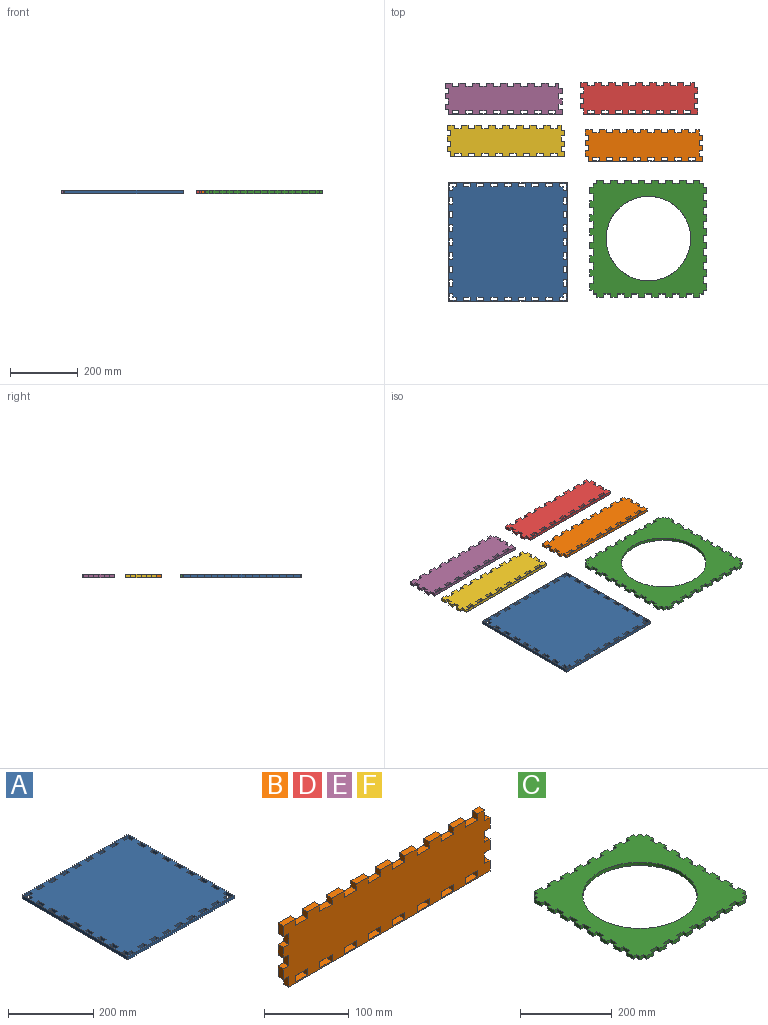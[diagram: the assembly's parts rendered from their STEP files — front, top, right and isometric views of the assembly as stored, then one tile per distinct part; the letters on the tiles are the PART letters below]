
ASSEMBLY  parts=6 mates=5
PART A: 142 faces, bbox 351x351x9 mm
  f0: plane 351x351mm, normal (0,0,1), area 116949.7mm2, adj f2,f3,f4,f5,f6,f7,f8,f9
  f1: plane 351x351mm, normal (0,0,-1), area 116949.7mm2, adj f2,f3,f4,f5,f6,f7,f8,f9
  f2: plane 11.29x9mm, normal (1,0,0), area 101.6mm2, adj f0,f1,f3,f4
  f3: plane 11.29x9mm, normal (0,1,0), area 101.6mm2, adj f0,f1,f2,f5
  f4: plane 9x9mm, normal (0,1,0), area 81mm2, adj f0,f1,f2,f110
  f5: plane 9x9mm, normal (1,0,0), area 81mm2, adj f0,f1,f3,f109
  f6: plane 20.29x9mm, normal (1,0,0), area 182.6mm2, adj f0,f1,f7,f8
  f7: plane 9x9mm, normal (0,1,0), area 81mm2, adj f0,f1,f6,f111
  f8: plane 9x9mm, normal (0,-1,0), area 81mm2, adj f0,f1,f6,f111
  f9: plane 20.29x9mm, normal (1,0,0), area 182.6mm2, adj f0,f1,f10,f11
  f10: plane 9x9mm, normal (0,1,0), area 81mm2, adj f0,f1,f9,f112
  f11: plane 9x9mm, normal (0,-1,0), area 81mm2, adj f0,f1,f9,f112
  f12: plane 20.29x9mm, normal (1,0,0), area 182.6mm2, adj f0,f1,f13,f14
  f13: plane 9x9mm, normal (0,1,0), area 81mm2, adj f0,f1,f12,f113
  f14: plane 9x9mm, normal (0,-1,0), area 81mm2, adj f0,f1,f12,f113
  f15: plane 20.29x9mm, normal (1,0,0), area 182.6mm2, adj f0,f1,f16,f17
  f16: plane 9x9mm, normal (0,1,0), area 81mm2, adj f0,f1,f15,f114
  f17: plane 9x9mm, normal (0,-1,0), area 81mm2, adj f0,f1,f15,f114
  f18: plane 20.29x9mm, normal (1,0,0), area 182.6mm2, adj f0,f1,f19,f20
  f19: plane 9x9mm, normal (0,1,0), area 81mm2, adj f0,f1,f18,f115
  f20: plane 9x9mm, normal (0,-1,0), area 81mm2, adj f0,f1,f18,f115
  f21: plane 20.29x9mm, normal (1,0,0), area 182.6mm2, adj f0,f1,f22,f23
  f22: plane 9x9mm, normal (0,1,0), area 81mm2, adj f0,f1,f21,f116
  f23: plane 9x9mm, normal (0,-1,0), area 81mm2, adj f0,f1,f21,f116
  f24: plane 20.29x9mm, normal (1,0,0), area 182.6mm2, adj f0,f1,f25,f26
  f25: plane 9x9mm, normal (0,1,0), area 81mm2, adj f0,f1,f24,f117
  f26: plane 9x9mm, normal (0,-1,0), area 81mm2, adj f0,f1,f24,f117
  f27: plane 11.29x9mm, normal (1,0,0), area 101.6mm2, adj f0,f1,f28,f30
  f28: plane 11.29x9mm, normal (0,-1,0), area 101.6mm2, adj f0,f1,f27,f29
  f29: plane 9x9mm, normal (1,0,0), area 81mm2, adj f0,f1,f28,f118
  f30: plane 9x9mm, normal (0,-1,0), area 81mm2, adj f0,f1,f27,f138
  f31: plane 11.29x9mm, normal (0,1,0), area 101.6mm2, adj f0,f1,f32,f33
  f32: plane 11.29x9mm, normal (-1,0,0), area 101.6mm2, adj f0,f1,f31,f34
  f33: plane 9x9mm, normal (-1,0,0), area 81mm2, adj f0,f1,f31,f137
  f34: plane 9x9mm, normal (0,1,0), area 81mm2, adj f0,f1,f32,f133
  f35: plane 20.29x9mm, normal (0,1,0), area 182.6mm2, adj f0,f1,f36,f37
  f36: plane 9x9mm, normal (-1,0,0), area 81mm2, adj f0,f1,f35,f102
  f37: plane 9x9mm, normal (1,0,0), area 81mm2, adj f0,f1,f35,f102
  f38: plane 20.29x9mm, normal (0,1,0), area 182.6mm2, adj f0,f1,f39,f40
  f39: plane 9x9mm, normal (-1,0,0), area 81mm2, adj f0,f1,f38,f103
  f40: plane 9x9mm, normal (1,0,0), area 81mm2, adj f0,f1,f38,f103
  f41: plane 20.29x9mm, normal (0,1,0), area 182.6mm2, adj f0,f1,f42,f43
  f42: plane 9x9mm, normal (-1,0,0), area 81mm2, adj f0,f1,f41,f104
  f43: plane 9x9mm, normal (1,0,0), area 81mm2, adj f0,f1,f41,f104
  f44: plane 20.29x9mm, normal (0,1,0), area 182.6mm2, adj f0,f1,f45,f46
  f45: plane 9x9mm, normal (-1,0,0), area 81mm2, adj f0,f1,f44,f105
  f46: plane 9x9mm, normal (1,0,0), area 81mm2, adj f0,f1,f44,f105
  f47: plane 20.29x9mm, normal (0,1,0), area 182.6mm2, adj f0,f1,f48,f49
  f48: plane 9x9mm, normal (-1,0,0), area 81mm2, adj f0,f1,f47,f106
  f49: plane 9x9mm, normal (1,0,0), area 81mm2, adj f0,f1,f47,f106
  f50: plane 20.29x9mm, normal (0,1,0), area 182.6mm2, adj f0,f1,f51,f52
  f51: plane 9x9mm, normal (-1,0,0), area 81mm2, adj f0,f1,f50,f107
  f52: plane 9x9mm, normal (1,0,0), area 81mm2, adj f0,f1,f50,f107
  f53: plane 20.29x9mm, normal (0,1,0), area 182.6mm2, adj f0,f1,f54,f55
  f54: plane 9x9mm, normal (-1,0,0), area 81mm2, adj f0,f1,f53,f108
  f55: plane 9x9mm, normal (1,0,0), area 81mm2, adj f0,f1,f53,f108
  f56: plane 20.29x9mm, normal (0,-1,0), area 182.6mm2, adj f0,f1,f57,f58
  f57: plane 9x9mm, normal (1,0,0), area 81mm2, adj f0,f1,f56,f119
  f58: plane 9x9mm, normal (-1,0,0), area 81mm2, adj f0,f1,f56,f119
  f59: plane 20.29x9mm, normal (0,-1,0), area 182.6mm2, adj f0,f1,f60,f61
  f60: plane 9x9mm, normal (1,0,0), area 81mm2, adj f0,f1,f59,f120
  f61: plane 9x9mm, normal (-1,0,0), area 81mm2, adj f0,f1,f59,f120
  f62: plane 20.29x9mm, normal (0,-1,0), area 182.6mm2, adj f0,f1,f63,f64
  f63: plane 9x9mm, normal (1,0,0), area 81mm2, adj f0,f1,f62,f121
  f64: plane 9x9mm, normal (-1,0,0), area 81mm2, adj f0,f1,f62,f121
  f65: plane 20.29x9mm, normal (0,-1,0), area 182.6mm2, adj f0,f1,f66,f67
  f66: plane 9x9mm, normal (1,0,0), area 81mm2, adj f0,f1,f65,f122
  f67: plane 9x9mm, normal (-1,0,0), area 81mm2, adj f0,f1,f65,f122
  f68: plane 20.29x9mm, normal (0,-1,0), area 182.6mm2, adj f0,f1,f69,f70
  f69: plane 9x9mm, normal (1,0,0), area 81mm2, adj f0,f1,f68,f123
  f70: plane 9x9mm, normal (-1,0,0), area 81mm2, adj f0,f1,f68,f123
  f71: plane 20.29x9mm, normal (0,-1,0), area 182.6mm2, adj f0,f1,f72,f73
  f72: plane 9x9mm, normal (1,0,0), area 81mm2, adj f0,f1,f71,f124
  f73: plane 9x9mm, normal (-1,0,0), area 81mm2, adj f0,f1,f71,f124
  f74: plane 20.29x9mm, normal (0,-1,0), area 182.6mm2, adj f0,f1,f75,f76
  f75: plane 9x9mm, normal (1,0,0), area 81mm2, adj f0,f1,f74,f125
  f76: plane 9x9mm, normal (-1,0,0), area 81mm2, adj f0,f1,f74,f125
  f77: plane 11.29x9mm, normal (0,-1,0), area 101.6mm2, adj f0,f1,f78,f80
  f78: plane 11.29x9mm, normal (-1,0,0), area 101.6mm2, adj f0,f1,f77,f79
  f79: plane 9x9mm, normal (0,-1,0), area 81mm2, adj f0,f1,f78,f140
  f80: plane 9x9mm, normal (-1,0,0), area 81mm2, adj f0,f1,f77,f139
  f81: plane 20.29x9mm, normal (-1,0,0), area 182.6mm2, adj f0,f1,f82,f83
  f82: plane 9x9mm, normal (0,-1,0), area 81mm2, adj f0,f1,f81,f126
  f83: plane 9x9mm, normal (0,1,0), area 81mm2, adj f0,f1,f81,f126
  f84: plane 20.29x9mm, normal (-1,0,0), area 182.6mm2, adj f0,f1,f85,f86
  f85: plane 9x9mm, normal (0,-1,0), area 81mm2, adj f0,f1,f84,f127
  f86: plane 9x9mm, normal (0,1,0), area 81mm2, adj f0,f1,f84,f127
  f87: plane 20.29x9mm, normal (-1,0,0), area 182.6mm2, adj f0,f1,f88,f89
  f88: plane 9x9mm, normal (0,-1,0), area 81mm2, adj f0,f1,f87,f128
  f89: plane 9x9mm, normal (0,1,0), area 81mm2, adj f0,f1,f87,f128
  f90: plane 20.29x9mm, normal (-1,0,0), area 182.6mm2, adj f0,f1,f91,f92
  f91: plane 9x9mm, normal (0,-1,0), area 81mm2, adj f0,f1,f90,f129
  f92: plane 9x9mm, normal (0,1,0), area 81mm2, adj f0,f1,f90,f129
  f93: plane 20.29x9mm, normal (-1,0,0), area 182.6mm2, adj f0,f1,f94,f95
  f94: plane 9x9mm, normal (0,-1,0), area 81mm2, adj f0,f1,f93,f130
  f95: plane 9x9mm, normal (0,1,0), area 81mm2, adj f0,f1,f93,f130
  f96: plane 20.29x9mm, normal (-1,0,0), area 182.6mm2, adj f0,f1,f97,f98
  f97: plane 9x9mm, normal (0,-1,0), area 81mm2, adj f0,f1,f96,f131
  f98: plane 9x9mm, normal (0,1,0), area 81mm2, adj f0,f1,f96,f131
  f99: plane 20.29x9mm, normal (-1,0,0), area 182.6mm2, adj f0,f1,f100,f101
  f100: plane 9x9mm, normal (0,1,0), area 81mm2, adj f0,f1,f99,f132
  f101: plane 9x9mm, normal (0,-1,0), area 81mm2, adj f0,f1,f99,f132
  f102: plane 20.29x9mm, normal (0,-1,0), area 182.6mm2, adj f0,f1,f36,f37
  f103: plane 20.29x9mm, normal (0,-1,0), area 182.6mm2, adj f0,f1,f39,f40
  f104: plane 20.29x9mm, normal (0,-1,0), area 182.6mm2, adj f0,f1,f42,f43
  f105: plane 20.29x9mm, normal (0,-1,0), area 182.6mm2, adj f0,f1,f45,f46
  f106: plane 20.29x9mm, normal (0,-1,0), area 182.6mm2, adj f0,f1,f48,f49
  f107: plane 20.29x9mm, normal (0,-1,0), area 182.6mm2, adj f0,f1,f51,f52
  f108: plane 20.29x9mm, normal (0,-1,0), area 182.6mm2, adj f0,f1,f54,f55
  f109: plane 20.29x9mm, normal (0,-1,0), area 182.6mm2, adj f0,f1,f5,f110
  f110: plane 20.29x9mm, normal (-1,0,0), area 182.6mm2, adj f0,f1,f4,f109
  f111: plane 20.29x9mm, normal (-1,0,0), area 182.6mm2, adj f0,f1,f7,f8
  f112: plane 20.29x9mm, normal (-1,0,0), area 182.6mm2, adj f0,f1,f10,f11
  f113: plane 20.29x9mm, normal (-1,0,0), area 182.6mm2, adj f0,f1,f13,f14
  f114: plane 20.29x9mm, normal (-1,0,0), area 182.6mm2, adj f0,f1,f16,f17
  f115: plane 20.29x9mm, normal (-1,0,0), area 182.6mm2, adj f0,f1,f19,f20
  f116: plane 20.29x9mm, normal (-1,0,0), area 182.6mm2, adj f0,f1,f22,f23
  f117: plane 20.29x9mm, normal (-1,0,0), area 182.6mm2, adj f0,f1,f25,f26
  f118: plane 20.29x9mm, normal (0,1,0), area 182.6mm2, adj f0,f1,f29,f138
  f119: plane 20.29x9mm, normal (0,1,0), area 182.6mm2, adj f0,f1,f57,f58
  f120: plane 20.29x9mm, normal (0,1,0), area 182.6mm2, adj f0,f1,f60,f61
  f121: plane 20.29x9mm, normal (0,1,0), area 182.6mm2, adj f0,f1,f63,f64
  f122: plane 20.29x9mm, normal (0,1,0), area 182.6mm2, adj f0,f1,f66,f67
  f123: plane 20.29x9mm, normal (0,1,0), area 182.6mm2, adj f0,f1,f69,f70
  f124: plane 20.29x9mm, normal (0,1,0), area 182.6mm2, adj f0,f1,f72,f73
  f125: plane 20.29x9mm, normal (0,1,0), area 182.6mm2, adj f0,f1,f75,f76
  f126: plane 20.29x9mm, normal (1,0,0), area 182.6mm2, adj f0,f1,f82,f83
  f127: plane 20.29x9mm, normal (1,0,0), area 182.6mm2, adj f0,f1,f85,f86
  f128: plane 20.29x9mm, normal (1,0,0), area 182.6mm2, adj f0,f1,f88,f89
  f129: plane 20.29x9mm, normal (1,0,0), area 182.6mm2, adj f0,f1,f91,f92
  f130: plane 20.29x9mm, normal (1,0,0), area 182.6mm2, adj f0,f1,f94,f95
  f131: plane 20.29x9mm, normal (1,0,0), area 182.6mm2, adj f0,f1,f97,f98
  f132: plane 20.29x9mm, normal (1,0,0), area 182.6mm2, adj f0,f1,f100,f101
  f133: plane 20.29x9mm, normal (1,0,0), area 182.6mm2, adj f0,f1,f34,f137
  f134: plane 351x9mm, normal (0,1,0), area 3159mm2, adj f0,f1,f135,f141
  f135: plane 351x9mm, normal (-1,0,0), area 3159mm2, adj f0,f1,f134,f136
  f136: plane 351x9mm, normal (0,-1,0), area 3159mm2, adj f0,f1,f135,f141
  f137: plane 20.29x9mm, normal (0,-1,0), area 182.6mm2, adj f0,f1,f33,f133
  f138: plane 20.29x9mm, normal (-1,0,0), area 182.6mm2, adj f0,f1,f30,f118
  f139: plane 20.29x9mm, normal (0,1,0), area 182.6mm2, adj f0,f1,f80,f140
  f140: plane 20.29x9mm, normal (1,0,0), area 182.6mm2, adj f0,f1,f79,f139
  f141: plane 351x9mm, normal (1,0,0), area 3159mm2, adj f0,f1,f134,f136
PART B: 90 faces, bbox 345.4x9x93.2 mm
  f0: plane 345.4x93.2mm, normal (0,-1,0), area 28379mm2, adj f1,f2,f3,f4,f5,f6,f7,f8
  f1: plane 15.7x9mm, normal (-1,0,0), area 141.3mm2, adj f0,f2,f56,f57
  f2: plane 9.2x9mm, normal (0,0,-1), area 82.8mm2, adj f0,f1,f3,f57
  f3: plane 15.5x9mm, normal (-1,0,0), area 139.5mm2, adj f0,f2,f4,f57
  f4: plane 9.2x9mm, normal (0,0,1), area 82.8mm2, adj f0,f3,f5,f57
  f5: plane 15.5x9mm, normal (-1,0,0), area 139.5mm2, adj f0,f4,f6,f57
  f6: plane 9.2x9mm, normal (0,0,-1), area 82.8mm2, adj f0,f5,f7,f57
  f7: plane 15.5x9mm, normal (-1,0,0), area 139.5mm2, adj f0,f6,f8,f57
  f8: plane 9.2x9mm, normal (0,0,1), area 82.8mm2, adj f0,f7,f9,f57
  f9: plane 15.5x9mm, normal (-1,0,0), area 139.5mm2, adj f0,f8,f10,f57
  f10: plane 9.2x9mm, normal (0,0,-1), area 82.8mm2, adj f0,f9,f11,f57
  f11: plane 15.5x9mm, normal (-1,0,0), area 139.5mm2, adj f0,f10,f12,f57
  f12: plane 336.2x9mm, normal (0,0,-1), area 3025.8mm2, adj f0,f11,f13,f57
  f13: plane 15.5x9mm, normal (1,0,0), area 139.5mm2, adj f0,f12,f14,f57
  f14: plane 9.2x9mm, normal (0,0,1), area 82.8mm2, adj f0,f13,f15,f57
  f15: plane 15.5x9mm, normal (1,0,0), area 139.5mm2, adj f0,f14,f16,f57
  f16: plane 9.2x9mm, normal (0,0,-1), area 82.8mm2, adj f0,f15,f17,f57
  f17: plane 15.5x9mm, normal (1,0,0), area 139.5mm2, adj f0,f16,f18,f57
  f18: plane 9.2x9mm, normal (0,0,1), area 82.8mm2, adj f0,f17,f19,f57
  f19: plane 15.5x9mm, normal (1,0,0), area 139.5mm2, adj f0,f18,f20,f57
  f20: plane 9.2x9mm, normal (0,0,-1), area 82.8mm2, adj f0,f19,f21,f57
  f21: plane 15.5x9mm, normal (1,0,0), area 139.5mm2, adj f0,f20,f22,f57
  f22: plane 9.2x9mm, normal (0,0,1), area 82.8mm2, adj f0,f21,f23,f57
  f23: plane 15.7x9mm, normal (1,0,0), area 141.3mm2, adj f0,f22,f24,f57
  f24: plane 11.29x9mm, normal (0,0,1), area 101.6mm2, adj f0,f23,f25,f57
  f25: plane 9.2x9mm, normal (-1,0,0), area 82.8mm2, adj f0,f24,f26,f57
  f26: plane 20.29x9mm, normal (0,0,1), area 182.6mm2, adj f0,f25,f27,f57
  f27: plane 9.2x9mm, normal (1,0,0), area 82.8mm2, adj f0,f26,f28,f57
  f28: plane 20.29x9mm, normal (0,0,1), area 182.6mm2, adj f0,f27,f29,f57
  f29: plane 9.2x9mm, normal (-1,0,0), area 82.8mm2, adj f0,f28,f30,f57
  f30: plane 20.29x9mm, normal (0,0,1), area 182.6mm2, adj f0,f29,f31,f57
  f31: plane 9.2x9mm, normal (1,0,0), area 82.8mm2, adj f0,f30,f32,f57
  f32: plane 20.29x9mm, normal (0,0,1), area 182.6mm2, adj f0,f31,f33,f57
  f33: plane 9.2x9mm, normal (-1,0,0), area 82.8mm2, adj f0,f32,f34,f57
  f34: plane 20.29x9mm, normal (0,0,1), area 182.6mm2, adj f0,f33,f35,f57
  f35: plane 9.2x9mm, normal (1,0,0), area 82.8mm2, adj f0,f34,f36,f57
  f36: plane 20.29x9mm, normal (0,0,1), area 182.6mm2, adj f0,f35,f37,f57
  f37: plane 9.2x9mm, normal (-1,0,0), area 82.8mm2, adj f0,f36,f38,f57
  f38: plane 20.29x9mm, normal (0,0,1), area 182.6mm2, adj f0,f37,f39,f57
  f39: plane 9.2x9mm, normal (1,0,0), area 82.8mm2, adj f0,f38,f40,f57
  f40: plane 20.29x9mm, normal (0,0,1), area 182.6mm2, adj f0,f39,f41,f57
  f41: plane 9.2x9mm, normal (-1,0,0), area 82.8mm2, adj f0,f40,f42,f57
  f42: plane 20.29x9mm, normal (0,0,1), area 182.6mm2, adj f0,f41,f43,f57
  f43: plane 9.2x9mm, normal (1,0,0), area 82.8mm2, adj f0,f42,f44,f57
  f44: plane 20.29x9mm, normal (0,0,1), area 182.6mm2, adj f0,f43,f45,f57
  f45: plane 9.2x9mm, normal (-1,0,0), area 82.8mm2, adj f0,f44,f46,f57
  f46: plane 20.29x9mm, normal (0,0,1), area 182.6mm2, adj f0,f45,f47,f57
  f47: plane 9.2x9mm, normal (1,0,0), area 82.8mm2, adj f0,f46,f48,f57
  f48: plane 20.29x9mm, normal (0,0,1), area 182.6mm2, adj f0,f47,f49,f57
  f49: plane 9.2x9mm, normal (-1,0,0), area 82.8mm2, adj f0,f48,f50,f57
  f50: plane 20.29x9mm, normal (0,0,1), area 182.6mm2, adj f0,f49,f51,f57
  f51: plane 9.2x9mm, normal (1,0,0), area 82.8mm2, adj f0,f50,f52,f57
  f52: plane 20.29x9mm, normal (0,0,1), area 182.6mm2, adj f0,f51,f53,f57
  f53: plane 9.2x9mm, normal (-1,0,0), area 82.8mm2, adj f0,f52,f54,f57
  f54: plane 20.29x9mm, normal (0,0,1), area 182.6mm2, adj f0,f53,f55,f57
  f55: plane 9.2x9mm, normal (1,0,0), area 82.8mm2, adj f0,f54,f56,f57
  f56: plane 20.49x9mm, normal (0,0,1), area 184.4mm2, adj f0,f1,f55,f57
  f57: plane 345.4x93.2mm, normal (0,1,0), area 28379mm2, adj f1,f2,f3,f4,f5,f6,f7,f8
  f58: plane 9x9mm, normal (-1,0,0), area 81mm2, adj f0,f57,f60,f61
  f59: plane 9x9mm, normal (1,0,0), area 81mm2, adj f0,f57,f60,f61
  f60: plane 20.29x9mm, normal (0,0,1), area 182.6mm2, adj f0,f57,f58,f59
  f61: plane 20.29x9mm, normal (0,0,-1), area 182.6mm2, adj f0,f57,f58,f59
  f62: plane 9x9mm, normal (-1,0,0), area 81mm2, adj f0,f57,f64,f65
  f63: plane 9x9mm, normal (1,0,0), area 81mm2, adj f0,f57,f64,f65
  f64: plane 20.29x9mm, normal (0,0,1), area 182.6mm2, adj f0,f57,f62,f63
  f65: plane 20.29x9mm, normal (0,0,-1), area 182.6mm2, adj f0,f57,f62,f63
  f66: plane 9x9mm, normal (-1,0,0), area 81mm2, adj f0,f57,f68,f69
  f67: plane 9x9mm, normal (1,0,0), area 81mm2, adj f0,f57,f68,f69
  f68: plane 20.29x9mm, normal (0,0,1), area 182.6mm2, adj f0,f57,f66,f67
  f69: plane 20.29x9mm, normal (0,0,-1), area 182.6mm2, adj f0,f57,f66,f67
  f70: plane 9x9mm, normal (-1,0,0), area 81mm2, adj f0,f57,f72,f73
  f71: plane 9x9mm, normal (1,0,0), area 81mm2, adj f0,f57,f72,f73
  f72: plane 20.29x9mm, normal (0,0,1), area 182.6mm2, adj f0,f57,f70,f71
  f73: plane 20.29x9mm, normal (0,0,-1), area 182.6mm2, adj f0,f57,f70,f71
  f74: plane 9x9mm, normal (-1,0,0), area 81mm2, adj f0,f57,f76,f77
  f75: plane 9x9mm, normal (1,0,0), area 81mm2, adj f0,f57,f76,f77
  f76: plane 20.29x9mm, normal (0,0,1), area 182.6mm2, adj f0,f57,f74,f75
  f77: plane 20.29x9mm, normal (0,0,-1), area 182.6mm2, adj f0,f57,f74,f75
  f78: plane 9x9mm, normal (-1,0,0), area 81mm2, adj f0,f57,f80,f81
  f79: plane 9x9mm, normal (1,0,0), area 81mm2, adj f0,f57,f80,f81
  f80: plane 20.29x9mm, normal (0,0,1), area 182.6mm2, adj f0,f57,f78,f79
  f81: plane 20.29x9mm, normal (0,0,-1), area 182.6mm2, adj f0,f57,f78,f79
  f82: plane 9x9mm, normal (-1,0,0), area 81mm2, adj f0,f57,f84,f85
  f83: plane 9x9mm, normal (1,0,0), area 81mm2, adj f0,f57,f84,f85
  f84: plane 20.29x9mm, normal (0,0,1), area 182.6mm2, adj f0,f57,f82,f83
  f85: plane 20.29x9mm, normal (0,0,-1), area 182.6mm2, adj f0,f57,f82,f83
  f86: plane 20.29x9mm, normal (0,0,-1), area 182.6mm2, adj f0,f57,f88,f89
  f87: plane 20.29x9mm, normal (0,0,1), area 182.6mm2, adj f0,f57,f88,f89
  f88: plane 9x9mm, normal (-1,0,0), area 81mm2, adj f0,f57,f86,f87
  f89: plane 9x9mm, normal (1,0,0), area 81mm2, adj f0,f57,f86,f87
PART C: 135 faces, bbox 345.4x345.4x9 mm
  f0: plane 20.29x9mm, normal (1,0,0), area 182.6mm2, adj f32,f33,f36,f40
  f1: plane 20.29x9mm, normal (1,0,0), area 182.6mm2, adj f32,f33,f39,f43
  f2: plane 20.29x9mm, normal (1,0,0), area 182.6mm2, adj f32,f33,f42,f46
  f3: plane 20.29x9mm, normal (1,0,0), area 182.6mm2, adj f32,f33,f45,f49
  f4: plane 20.29x9mm, normal (1,0,0), area 182.6mm2, adj f32,f33,f48,f52
  f5: plane 20.29x9mm, normal (1,0,0), area 182.6mm2, adj f32,f33,f51,f55
  f6: plane 20.29x9mm, normal (1,0,0), area 182.6mm2, adj f32,f33,f54,f58
  f7: plane 20.29x9mm, normal (1,0,0), area 182.6mm2, adj f32,f33,f57,f62
  f8: plane 20.29x9mm, normal (0,1,0), area 182.6mm2, adj f32,f33,f65,f69
  f9: plane 20.29x9mm, normal (0,1,0), area 182.6mm2, adj f32,f33,f68,f72
  f10: plane 20.29x9mm, normal (0,1,0), area 182.6mm2, adj f32,f33,f71,f75
  f11: plane 20.29x9mm, normal (0,1,0), area 182.6mm2, adj f32,f33,f74,f78
  f12: plane 20.29x9mm, normal (0,1,0), area 182.6mm2, adj f32,f33,f77,f81
  f13: plane 20.29x9mm, normal (0,1,0), area 182.6mm2, adj f32,f33,f80,f84
  f14: plane 20.29x9mm, normal (0,1,0), area 182.6mm2, adj f32,f33,f83,f87
  f15: plane 20.29x9mm, normal (0,1,0), area 182.6mm2, adj f32,f33,f37,f86
  f16: plane 20.29x9mm, normal (-1,0,0), area 182.6mm2, adj f32,f33,f111,f115
  f17: plane 20.29x9mm, normal (-1,0,0), area 182.6mm2, adj f32,f33,f114,f118
  f18: plane 20.29x9mm, normal (-1,0,0), area 182.6mm2, adj f32,f33,f117,f121
  f19: plane 20.29x9mm, normal (-1,0,0), area 182.6mm2, adj f32,f33,f120,f124
  f20: plane 20.29x9mm, normal (-1,0,0), area 182.6mm2, adj f32,f33,f123,f127
  f21: plane 20.29x9mm, normal (-1,0,0), area 182.6mm2, adj f32,f33,f126,f130
  f22: plane 20.29x9mm, normal (-1,0,0), area 182.6mm2, adj f32,f33,f129,f132
  f23: plane 20.29x9mm, normal (-1,0,0), area 182.6mm2, adj f32,f33,f66,f133
  f24: plane 20.29x9mm, normal (0,-1,0), area 182.6mm2, adj f32,f33,f61,f90
  f25: plane 20.29x9mm, normal (0,-1,0), area 182.6mm2, adj f32,f33,f89,f93
  f26: plane 20.29x9mm, normal (0,-1,0), area 182.6mm2, adj f32,f33,f92,f96
  f27: plane 20.29x9mm, normal (0,-1,0), area 182.6mm2, adj f32,f33,f95,f99
  f28: plane 20.29x9mm, normal (0,-1,0), area 182.6mm2, adj f32,f33,f98,f102
  f29: plane 20.29x9mm, normal (0,-1,0), area 182.6mm2, adj f32,f33,f101,f105
  f30: plane 20.29x9mm, normal (0,-1,0), area 182.6mm2, adj f32,f33,f104,f108
  f31: plane 20.29x9mm, normal (0,-1,0), area 182.6mm2, adj f32,f33,f107,f112
  f32: plane 345.4x345.4mm, normal (0,0,1), area 63816.2mm2, adj f0,f1,f2,f3,f4,f5,f6,f7
  f33: plane 345.4x345.4mm, normal (0,0,-1), area 63816.2mm2, adj f0,f1,f2,f3,f4,f5,f6,f7
  f34: plane 11.29x9mm, normal (1,0,0), area 101.6mm2, adj f32,f33,f35,f36
  f35: plane 11.29x9mm, normal (0,1,0), area 101.6mm2, adj f32,f33,f34,f37
  f36: plane 9.2x9mm, normal (0,1,0), area 82.8mm2, adj f0,f32,f33,f34
  f37: plane 9.2x9mm, normal (1,0,0), area 82.8mm2, adj f15,f32,f33,f35
  f38: plane 20.29x9mm, normal (1,0,0), area 182.6mm2, adj f32,f33,f39,f40
  f39: plane 9.2x9mm, normal (0,1,0), area 82.8mm2, adj f1,f32,f33,f38
  f40: plane 9.2x9mm, normal (0,-1,0), area 82.8mm2, adj f0,f32,f33,f38
  f41: plane 20.29x9mm, normal (1,0,0), area 182.6mm2, adj f32,f33,f42,f43
  f42: plane 9.2x9mm, normal (0,1,0), area 82.8mm2, adj f2,f32,f33,f41
  f43: plane 9.2x9mm, normal (0,-1,0), area 82.8mm2, adj f1,f32,f33,f41
  f44: plane 20.29x9mm, normal (1,0,0), area 182.6mm2, adj f32,f33,f45,f46
  f45: plane 9.2x9mm, normal (0,1,0), area 82.8mm2, adj f3,f32,f33,f44
  f46: plane 9.2x9mm, normal (0,-1,0), area 82.8mm2, adj f2,f32,f33,f44
  f47: plane 20.29x9mm, normal (1,0,0), area 182.6mm2, adj f32,f33,f48,f49
  f48: plane 9.2x9mm, normal (0,1,0), area 82.8mm2, adj f4,f32,f33,f47
  f49: plane 9.2x9mm, normal (0,-1,0), area 82.8mm2, adj f3,f32,f33,f47
  f50: plane 20.29x9mm, normal (1,0,0), area 182.6mm2, adj f32,f33,f51,f52
  f51: plane 9.2x9mm, normal (0,1,0), area 82.8mm2, adj f5,f32,f33,f50
  f52: plane 9.2x9mm, normal (0,-1,0), area 82.8mm2, adj f4,f32,f33,f50
  f53: plane 20.29x9mm, normal (1,0,0), area 182.6mm2, adj f32,f33,f54,f55
  f54: plane 9.2x9mm, normal (0,1,0), area 82.8mm2, adj f6,f32,f33,f53
  f55: plane 9.2x9mm, normal (0,-1,0), area 82.8mm2, adj f5,f32,f33,f53
  f56: plane 20.29x9mm, normal (1,0,0), area 182.6mm2, adj f32,f33,f57,f58
  f57: plane 9.2x9mm, normal (0,1,0), area 82.8mm2, adj f7,f32,f33,f56
  f58: plane 9.2x9mm, normal (0,-1,0), area 82.8mm2, adj f6,f32,f33,f56
  f59: plane 11.29x9mm, normal (1,0,0), area 101.6mm2, adj f32,f33,f60,f62
  f60: plane 11.29x9mm, normal (0,-1,0), area 101.6mm2, adj f32,f33,f59,f61
  f61: plane 9.2x9mm, normal (1,0,0), area 82.8mm2, adj f24,f32,f33,f60
  f62: plane 9.2x9mm, normal (0,-1,0), area 82.8mm2, adj f7,f32,f33,f59
  f63: plane 11.29x9mm, normal (0,1,0), area 101.6mm2, adj f32,f33,f64,f65
  f64: plane 11.29x9mm, normal (-1,0,0), area 101.6mm2, adj f32,f33,f63,f66
  f65: plane 9.2x9mm, normal (-1,0,0), area 82.8mm2, adj f8,f32,f33,f63
  f66: plane 9.2x9mm, normal (0,1,0), area 82.8mm2, adj f23,f32,f33,f64
  f67: plane 20.29x9mm, normal (0,1,0), area 182.6mm2, adj f32,f33,f68,f69
  f68: plane 9.2x9mm, normal (-1,0,0), area 82.8mm2, adj f9,f32,f33,f67
  f69: plane 9.2x9mm, normal (1,0,0), area 82.8mm2, adj f8,f32,f33,f67
  f70: plane 20.29x9mm, normal (0,1,0), area 182.6mm2, adj f32,f33,f71,f72
  f71: plane 9.2x9mm, normal (-1,0,0), area 82.8mm2, adj f10,f32,f33,f70
  f72: plane 9.2x9mm, normal (1,0,0), area 82.8mm2, adj f9,f32,f33,f70
  f73: plane 20.29x9mm, normal (0,1,0), area 182.6mm2, adj f32,f33,f74,f75
  f74: plane 9.2x9mm, normal (-1,0,0), area 82.8mm2, adj f11,f32,f33,f73
  f75: plane 9.2x9mm, normal (1,0,0), area 82.8mm2, adj f10,f32,f33,f73
  f76: plane 20.29x9mm, normal (0,1,0), area 182.6mm2, adj f32,f33,f77,f78
  f77: plane 9.2x9mm, normal (-1,0,0), area 82.8mm2, adj f12,f32,f33,f76
  f78: plane 9.2x9mm, normal (1,0,0), area 82.8mm2, adj f11,f32,f33,f76
  f79: plane 20.29x9mm, normal (0,1,0), area 182.6mm2, adj f32,f33,f80,f81
  f80: plane 9.2x9mm, normal (-1,0,0), area 82.8mm2, adj f13,f32,f33,f79
  f81: plane 9.2x9mm, normal (1,0,0), area 82.8mm2, adj f12,f32,f33,f79
  f82: plane 20.29x9mm, normal (0,1,0), area 182.6mm2, adj f32,f33,f83,f84
  f83: plane 9.2x9mm, normal (-1,0,0), area 82.8mm2, adj f14,f32,f33,f82
  f84: plane 9.2x9mm, normal (1,0,0), area 82.8mm2, adj f13,f32,f33,f82
  f85: plane 20.29x9mm, normal (0,1,0), area 182.6mm2, adj f32,f33,f86,f87
  f86: plane 9.2x9mm, normal (-1,0,0), area 82.8mm2, adj f15,f32,f33,f85
  f87: plane 9.2x9mm, normal (1,0,0), area 82.8mm2, adj f14,f32,f33,f85
  f88: plane 20.29x9mm, normal (0,-1,0), area 182.6mm2, adj f32,f33,f89,f90
  f89: plane 9.2x9mm, normal (1,0,0), area 82.8mm2, adj f25,f32,f33,f88
  f90: plane 9.2x9mm, normal (-1,0,0), area 82.8mm2, adj f24,f32,f33,f88
  f91: plane 20.29x9mm, normal (0,-1,0), area 182.6mm2, adj f32,f33,f92,f93
  f92: plane 9.2x9mm, normal (1,0,0), area 82.8mm2, adj f26,f32,f33,f91
  f93: plane 9.2x9mm, normal (-1,0,0), area 82.8mm2, adj f25,f32,f33,f91
  f94: plane 20.29x9mm, normal (0,-1,0), area 182.6mm2, adj f32,f33,f95,f96
  f95: plane 9.2x9mm, normal (1,0,0), area 82.8mm2, adj f27,f32,f33,f94
  f96: plane 9.2x9mm, normal (-1,0,0), area 82.8mm2, adj f26,f32,f33,f94
  f97: plane 20.29x9mm, normal (0,-1,0), area 182.6mm2, adj f32,f33,f98,f99
  f98: plane 9.2x9mm, normal (1,0,0), area 82.8mm2, adj f28,f32,f33,f97
  f99: plane 9.2x9mm, normal (-1,0,0), area 82.8mm2, adj f27,f32,f33,f97
  f100: plane 20.29x9mm, normal (0,-1,0), area 182.6mm2, adj f32,f33,f101,f102
  f101: plane 9.2x9mm, normal (1,0,0), area 82.8mm2, adj f29,f32,f33,f100
  f102: plane 9.2x9mm, normal (-1,0,0), area 82.8mm2, adj f28,f32,f33,f100
  f103: plane 20.29x9mm, normal (0,-1,0), area 182.6mm2, adj f32,f33,f104,f105
  f104: plane 9.2x9mm, normal (1,0,0), area 82.8mm2, adj f30,f32,f33,f103
  f105: plane 9.2x9mm, normal (-1,0,0), area 82.8mm2, adj f29,f32,f33,f103
  f106: plane 20.29x9mm, normal (0,-1,0), area 182.6mm2, adj f32,f33,f107,f108
  f107: plane 9.2x9mm, normal (1,0,0), area 82.8mm2, adj f31,f32,f33,f106
  f108: plane 9.2x9mm, normal (-1,0,0), area 82.8mm2, adj f30,f32,f33,f106
  f109: plane 11.29x9mm, normal (0,-1,0), area 101.6mm2, adj f32,f33,f110,f112
  f110: plane 11.29x9mm, normal (-1,0,0), area 101.6mm2, adj f32,f33,f109,f111
  f111: plane 9.2x9mm, normal (0,-1,0), area 82.8mm2, adj f16,f32,f33,f110
  f112: plane 9.2x9mm, normal (-1,0,0), area 82.8mm2, adj f31,f32,f33,f109
  f113: plane 20.29x9mm, normal (-1,0,0), area 182.6mm2, adj f32,f33,f114,f115
  f114: plane 9.2x9mm, normal (0,-1,0), area 82.8mm2, adj f17,f32,f33,f113
  f115: plane 9.2x9mm, normal (0,1,0), area 82.8mm2, adj f16,f32,f33,f113
  f116: plane 20.29x9mm, normal (-1,0,0), area 182.6mm2, adj f32,f33,f117,f118
  f117: plane 9.2x9mm, normal (0,-1,0), area 82.8mm2, adj f18,f32,f33,f116
  f118: plane 9.2x9mm, normal (0,1,0), area 82.8mm2, adj f17,f32,f33,f116
  f119: plane 20.29x9mm, normal (-1,0,0), area 182.6mm2, adj f32,f33,f120,f121
  f120: plane 9.2x9mm, normal (0,-1,0), area 82.8mm2, adj f19,f32,f33,f119
  f121: plane 9.2x9mm, normal (0,1,0), area 82.8mm2, adj f18,f32,f33,f119
  f122: plane 20.29x9mm, normal (-1,0,0), area 182.6mm2, adj f32,f33,f123,f124
  f123: plane 9.2x9mm, normal (0,-1,0), area 82.8mm2, adj f20,f32,f33,f122
  f124: plane 9.2x9mm, normal (0,1,0), area 82.8mm2, adj f19,f32,f33,f122
  f125: plane 20.29x9mm, normal (-1,0,0), area 182.6mm2, adj f32,f33,f126,f127
  f126: plane 9.2x9mm, normal (0,-1,0), area 82.8mm2, adj f21,f32,f33,f125
  f127: plane 9.2x9mm, normal (0,1,0), area 82.8mm2, adj f20,f32,f33,f125
  f128: plane 20.29x9mm, normal (-1,0,0), area 182.6mm2, adj f32,f33,f129,f130
  f129: plane 9.2x9mm, normal (0,-1,0), area 82.8mm2, adj f22,f32,f33,f128
  f130: plane 9.2x9mm, normal (0,1,0), area 82.8mm2, adj f21,f32,f33,f128
  f131: plane 20.29x9mm, normal (-1,0,0), area 182.6mm2, adj f32,f33,f132,f133
  f132: plane 9.2x9mm, normal (0,1,0), area 82.8mm2, adj f22,f32,f33,f131
  f133: plane 9.2x9mm, normal (0,-1,0), area 82.8mm2, adj f23,f32,f33,f131
  f134: cylinder r=125mm len=250mm, axis (0,0,-1), area 7068.6mm2, adj f32,f33
PART D: same geometry as B
PART E: same geometry as B
PART F: same geometry as B
PLACE A t=(-115.27,-104.67,-158.67)mm fixed
PLACE B rot(axis=(-1,0,0),90deg) t=(286.29,120.28,-225.17)mm
PLACE C t=(299.5,-94.68,-76.67)mm
PLACE D rot(axis=(-1,0,0),90deg) t=(272.52,259.93,-225.17)mm
PLACE E rot(axis=(-1,0,0),90deg) t=(-127.95,258.28,-225.17)mm
PLACE F rot(axis=(-1,0,0),90deg) t=(-121.27,133.39,-225.17)mm
MATE planar F.f0 <-> E.f0  axis (0,0,1) through (-121.28,192.84,-52.67)mm
MATE planar C.f134 <-> A.f0  axis (0,0,1) through (299.5,-94.68,-52.67)mm
MATE planar E.f0 <-> A.f0  axis (0,0,1) through (-127.96,317.73,-52.67)mm
MATE planar B.f0 <-> A.f0  axis (0,0,1) through (286.28,179.74,-52.67)mm
MATE planar D.f0 <-> F.f0  axis (0,0,1) through (272.51,319.38,-52.67)mm
